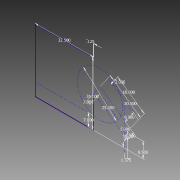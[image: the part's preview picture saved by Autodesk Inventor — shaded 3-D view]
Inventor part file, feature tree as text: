
AUTODESK INVENTOR PART (.ipt)
format: ipt  version: 2014 (Build 180170000, 170)  size: 79,872 bytes
history: native  units: in
note: dims shown in document units (in); Inventor stores cm internally (conversion verified against a paired STEP export)
features: sketch x1
ambient origin geometry x8: Origin, YZ Plane, XZ Plane, XY Plane, X Axis, Y Axis, Z Axis, Center Point
feature tree (1):
  sketch  "Sketch1"  dims[d0=32.5in d1=35.0in d2=7.0in d3=25.0in d5=6.0in d6=0.2405in d7=2.0in d8=20.5in d9=1.0in d10=8.5in d11=1.375in d12=0.125in d13=8.0in d14=18.0in d15=2.0in]
